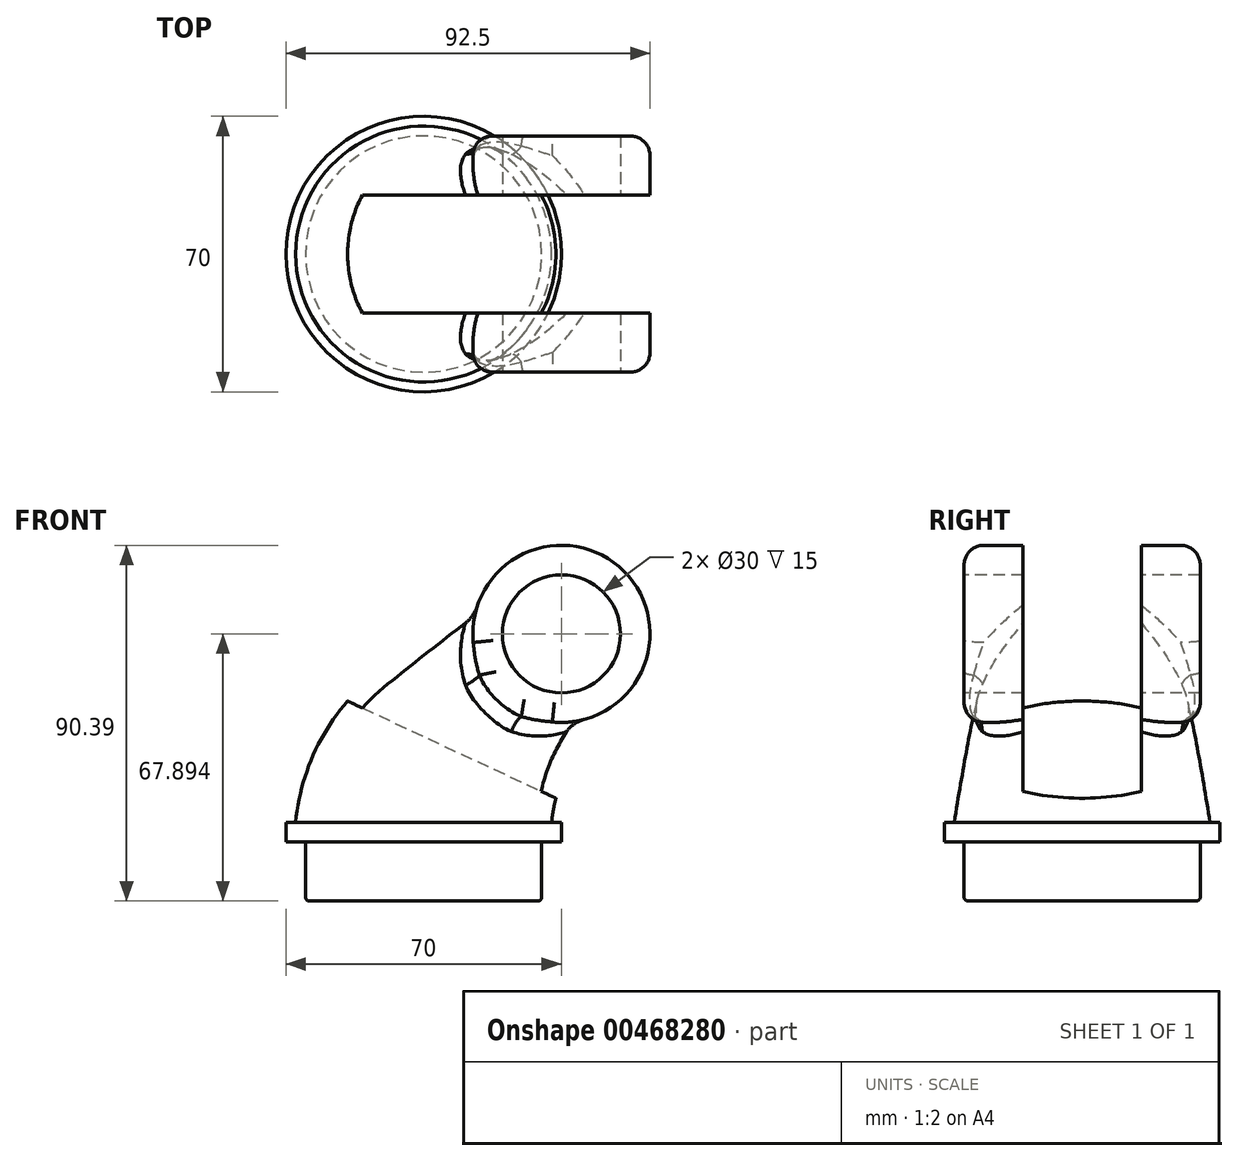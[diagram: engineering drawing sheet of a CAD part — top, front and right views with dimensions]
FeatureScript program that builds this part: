
annotation { "Feature Type Name" : "Feature", "Feature Type Description" : "" }
export const myFeature = defineFeature(function(context is Context, id is Id, definition is map)
    precondition{}
    {
        {
            var Q0;
            Q0=qCreatedBy(makeId("Top.planeOp"),FACE);
            var sketch = newSketch(context, id + "F0", { "sketchPlane" : qUnion([Q0])});
            skCircle(sketch, "E0", {"center": v(0, 0) * mm, "radius": 35 * mm});
            skSolve(sketch);
        }
        {
            var Q0;
            Q0=makeQuery(id+"F0.imprint","IMPRINT",FACE,{"disambiguationData":[TD([[makeQuery(id+"F0.imprint","IMPRINT",EDGE,{"derivedFrom":sQuery(id+"F0.wireOp",EDGE,"E0")}),1.0]])]});
            extrude(context, id + "F1", {"entities" : qUnion([Q0]), "depth" : 5 * mm});
        }
        {
            var Q0;
            Q0=qCreatedBy(makeId("Front.planeOp"),FACE);
            var sketch = newSketch(context, id + "F2", { "sketchPlane" : qUnion([Q0])});
            skArc(sketch, "E1", {"start": v(17.6, 38.3) * mm, "mid": v(5.55, 23.37) * mm, "end": v(0, 5) * mm});
            skLineSegment(sketch, "E2", {"start": v(17.6, 38.3) * mm, "end": v(35, 52.9) * mm});
            skSolve(sketch);
        }
        {
            var Q0;
            Q0=sQuery(id+"F2.wireOp",EDGE,"E2");
            var Q1;
            Q1=sQuery(id+"F2.wireOp",VERTEX,"E2.end");
            cPlane(context, id + "F3", {"entities" : qUnion([Q0, Q1]), "cplaneType" : CPlaneType.LINE_POINT, "offset" : 25 * mm, "width" : 150 * mm, "height" : 150 * mm});
        }
        {
            var Q0;
            Q0=qCreatedBy(id+"F3.planeOp",FACE);
            var sketch = newSketch(context, id + "F4", { "sketchPlane" : qUnion([Q0])});
            skCircle(sketch, "E3", {"center": v(0, 18.02) * mm, "radius": 22.5 * mm});
            skSolve(sketch);
        }
        {
            var Q0;
            Q0=makeQuery(id+"F1.opExtrude","CAP_FACE",FACE,{"disambiguationData":[OSD([sQuery(id+"F0.wireOp",EDGE,"E0")])],"isStart":false});
            var sketch = newSketch(context, id + "F5", { "sketchPlane" : qUnion([Q0])});
            skCircle(sketch, "E4", {"center": v(0, 0) * mm, "radius": 32.5 * mm});
            skSolve(sketch);
        }
        {
            var Q0;
            Q0=qCreatedBy(makeId("Front.planeOp"),FACE);
            var sketch = newSketch(context, id + "F6", { "sketchPlane" : qUnion([Q0])});
            skArc(sketch, "E5", {"start": v(-13.25, 41.78) * mm, "mid": v(-26.5, 25.3) * mm, "end": v(-32.5, 5) * mm});
            skLineSegment(sketch, "E6", {"start": v(-13.25, 41.78) * mm, "end": v(20.54, 70.13) * mm});
            skSolve(sketch);
        }
        {
            var Q0;
            Q0=qCreatedBy(makeId("Front.planeOp"),FACE);
            var sketch = newSketch(context, id + "F7", { "sketchPlane" : qUnion([Q0])});
            skArc(sketch, "E7", {"start": v(48.46, 34.82) * mm, "mid": v(37.6, 21.45) * mm, "end": v(32.5, 5) * mm});
            skLineSegment(sketch, "E8", {"start": v(48.46, 34.82) * mm, "end": v(49.46, 35.66) * mm});
            skSolve(sketch);
        }
        {
            var Q1;
            Q1=makeQuery(id+"F4.imprint","IMPRINT",FACE,{"disambiguationData":[TD([[makeQuery(id+"F4.imprint","IMPRINT",EDGE,{"derivedFrom":sQuery(id+"F4.wireOp",EDGE,"E3")}),1.0]])]});
            var Q2;
            Q2=makeQuery(id+"F5.imprint","IMPRINT",FACE,{"disambiguationData":[TD([[makeQuery(id+"F5.imprint","IMPRINT",EDGE,{"derivedFrom":sQuery(id+"F5.wireOp",EDGE,"E4")}),1.0]])]});
            var Q3;
            Q3=qConstructionFilter(qBodyType(qCreatedBy(id+"F6",EDGE),BodyType.WIRE),ConstructionObject.NO);
            var Q4;
            Q4=qConstructionFilter(qBodyType(qCreatedBy(id+"F7",EDGE),BodyType.WIRE),ConstructionObject.NO);
            loft(context, id + "F8", {"operationType" : NewBodyOperationType.ADD, "addGuides" : true, "sheetProfilesArray" : [{ "sheetProfileEntities" : qUnion([Q1]) }, { "sheetProfileEntities" : qUnion([Q2]) }], "guidesArray" : [{ "guideEntities" : qUnion([Q3]), "guideDerivativeType" : LoftGuideDerivativeType.DEFAULT, "guideDerivativeMagnitude" : 1 }, { "guideEntities" : qUnion([Q4]), "guideDerivativeType" : LoftGuideDerivativeType.DEFAULT, "guideDerivativeMagnitude" : 1 }]});
        }
        {
            var Q0;
            Q0=qCreatedBy(makeId("Front.planeOp"),FACE);
            var sketch = newSketch(context, id + "F9", { "sketchPlane" : qUnion([Q0])});
            skCircle(sketch, "E9", {"center": v(35, 52.9) * mm, "radius": 22.5 * mm});
            skSolve(sketch);
        }
        {
            var Q0;
            Q0=qSketchRegion(id+"F9",true);
            extrude(context, id + "F10", {"entities" : qUnion([Q0]), "operationType" : NewBodyOperationType.ADD, "endBound" : BoundingType.SYMMETRIC, "depth" : 60 * mm});
        }
        {
            var Q0;
            Q0=makeQuery(id+"F10.boolean.opBoolean","INTERSECT",EDGE,{"disambiguationData":[OD(1.0)],"derivedFrom":[makeQuery(id+"F8.opLoft","SWEPT_FACE",FACE,{"disambiguationData":[OSD([sQuery(id+"F4.wireOp",EDGE,"E3"),sQuery(id+"F5.wireOp",EDGE,"E4"),sQuery(id+"F6.wireOp",VERTEX,"E6.start"),sQuery(id+"F6.wireOp",EDGE,"E5"),sQuery(id+"F6.wireOp",EDGE,"E6"),sQuery(id+"F7.wireOp",VERTEX,"E8.start"),sQuery(id+"F7.wireOp",EDGE,"E7"),sQuery(id+"F7.wireOp",EDGE,"E8")])]}),makeQuery(id+"F10.opExtrude","SWEPT_FACE",FACE,{"disambiguationData":[OSD([sQuery(id+"F9.wireOp",EDGE,"E9")])]})]});
            var Q1;
            Q1=makeQuery(id+"F10.boolean.opBoolean","INTERSECT",EDGE,{"disambiguationData":[OD(0.0)],"derivedFrom":[makeQuery(id+"F8.opLoft","SWEPT_FACE",FACE,{"disambiguationData":[OSD([sQuery(id+"F4.wireOp",EDGE,"E3"),sQuery(id+"F5.wireOp",EDGE,"E4"),sQuery(id+"F6.wireOp",VERTEX,"E6.start"),sQuery(id+"F6.wireOp",EDGE,"E5"),sQuery(id+"F6.wireOp",EDGE,"E6"),sQuery(id+"F7.wireOp",VERTEX,"E8.start"),sQuery(id+"F7.wireOp",EDGE,"E7"),sQuery(id+"F7.wireOp",EDGE,"E8")])]}),makeQuery(id+"F10.opExtrude","SWEPT_FACE",FACE,{"disambiguationData":[OSD([sQuery(id+"F9.wireOp",EDGE,"E9")])]})]});
            fillet(context, id + "F11", {"entities" : qUnion([Q0, Q1]), "radius" : 5 * mm, "tangentPropagation" : true, "allowEdgeOverflow" : false});
        }
        {
            var Q0;
            Q0=makeQuery(id+"F10.opExtrude","CAP_FACE",FACE,{"disambiguationData":[OSD([sQuery(id+"F9.wireOp",EDGE,"E9")])],"isStart":false});
            var Q1;
            Q1=makeQuery(id+"F10.opExtrude","CAP_FACE",FACE,{"disambiguationData":[OSD([sQuery(id+"F9.wireOp",EDGE,"E9")])],"isStart":true});
            fillet(context, id + "F12", {"entities" : qUnion([Q0, Q1]), "radius" : 5 * mm, "tangentPropagation" : true, "allowEdgeOverflow" : false});
        }
        {
            var Q0;
            Q0=makeQuery(id+"F10.opExtrude","CAP_FACE",FACE,{"disambiguationData":[OSD([sQuery(id+"F9.wireOp",EDGE,"E9")])],"isStart":false});
            var sketch = newSketch(context, id + "F13", { "sketchPlane" : qUnion([Q0])});
            skCircle(sketch, "E10", {"center": v(35, 52.9) * mm, "radius": 15 * mm});
            skSolve(sketch);
        }
        {
            var Q0;
            Q0=makeQuery(id+"F13.imprint","IMPRINT",FACE,{"disambiguationData":[TD([[makeQuery(id+"F13.imprint","IMPRINT",EDGE,{"derivedFrom":sQuery(id+"F13.wireOp",EDGE,"E10")}),1.0]])]});
            extrude(context, id + "F14", {"entities" : qUnion([Q0]), "operationType" : NewBodyOperationType.REMOVE, "endBound" : BoundingType.THROUGH_ALL, "oppositeDirection" : true, "depth" : 25 * mm});
        }
        {
            var Q0;
            Q0=qCreatedBy(makeId("Front.planeOp"),FACE);
            var sketch = newSketch(context, id + "F15", { "sketchPlane" : qUnion([Q0])});
            skLineSegment(sketch, "E11", {"start": v(-104.18, 75.4) * mm, "end": v(57.5, 0) * mm});
            skLineSegment(sketch, "E12", {"start": v(57.5, 75.4) * mm, "end": v(57.5, 0) * mm});
            skLineSegment(sketch, "E13", {"start": v(57.5, 75.4) * mm, "end": v(-104.18, 75.4) * mm});
            skSolve(sketch);
        }
        {
            var Q0;
            Q0=makeQuery(id+"F15.imprint","IMPRINT",FACE,{"disambiguationData":[TD([[makeQuery(id+"F15.imprint","IMPRINT",EDGE,{"derivedFrom":sQuery(id+"F15.wireOp",EDGE,"E11")}),1.0]])]});
            extrude(context, id + "F16", {"entities" : qUnion([Q0]), "operationType" : NewBodyOperationType.REMOVE, "endBound" : BoundingType.SYMMETRIC, "oppositeDirection" : true, "depth" : 30 * mm});
        }
        {
            var Q0;
            Q0=qCreatedBy(makeId("Front.planeOp"),FACE);
            var sketch = newSketch(context, id + "F17", { "sketchPlane" : qUnion([Q0])});
            skLineSegment(sketch, "E14.bottom", {"start": v(0, 0) * mm, "end": v(-30, 0) * mm});
            skLineSegment(sketch, "E14.top", {"start": v(0, -15) * mm, "end": v(-30, -15) * mm});
            skLineSegment(sketch, "E14.left", {"start": v(0, 0) * mm, "end": v(0, -15) * mm});
            skLineSegment(sketch, "E14.right", {"start": v(-30, 0) * mm, "end": v(-30, -15) * mm});
            skSolve(sketch);
        }
        {
            var Q0;
            Q0=makeQuery(id+"F17.imprint","IMPRINT",FACE,{"disambiguationData":[TD([[makeQuery(id+"F17.imprint","IMPRINT",EDGE,{"derivedFrom":sQuery(id+"F17.wireOp",EDGE,"E14.bottom")}),1.0]])]});
            var Q1;
            Q1=sQuery(id+"F17.wireOp",EDGE,"E14.left");
            revolve(context, id + "F18", {"operationType" : NewBodyOperationType.ADD, "entities" : qUnion([Q0]), "axis" : qUnion([Q1]), "revolveType" : RevolveType.FULL});
        }
        {
            var Q0;
            Q0=makeQuery(id+"F18.opRevolve","SWEPT_EDGE",EDGE,{"disambiguationData":[OSD([sQuery(id+"F17.wireOp",EDGE,"E14.top"),sQuery(id+"F17.wireOp",EDGE,"E14.right")])]});
            var Q1;
            Q1=makeQuery(id+"F18.opRevolve","SWEPT_EDGE",EDGE,{"disambiguationData":[OSD([sQuery(id+"F17.wireOp",EDGE,"E14.bottom"),sQuery(id+"F17.wireOp",EDGE,"E14.right")])]});
            fillet(context, id + "F19", {"entities" : qUnion([Q0, Q1]), "radius" : 1 * mm, "tangentPropagation" : true, "allowEdgeOverflow" : false});
        }
    });
